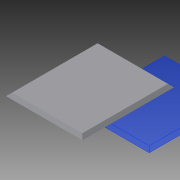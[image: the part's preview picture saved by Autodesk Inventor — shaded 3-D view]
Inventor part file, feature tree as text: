
AUTODESK INVENTOR PART (.ipt)
format: ipt  version: 2018.2 (Build 222227000, 227)  size: 75,776 bytes
history: native  units: mm
features: other x3, sketch x1
ambient origin geometry x8: Origin, YZ Plane, XZ Plane, XY Plane, X Axis, Y Axis, Z Axis, Center Point
bodies: Volumenkörper1 (feature_tree)
feature tree (4):
  other  "Wand1.ipt"
  other  "Volumenkörper1::Wand1.ipt"
  other  "Bezeichnung1"
  sketch  "Skizze1"  dims[d0=10.0mm]
